AUTODESK INVENTOR PART (.ipt)
format: ipt  version: 2015 (Build 190159000, 159)  size: 452,096 bytes
history: native  units: mm
features: other x24, loft x2, pattern_circular x2, sketch x1
ambient origin geometry x6: Origin, XZ Plane, X Axis, Y Axis, Z Axis, Center Point
bodies: Solid1 (feature_tree)
feature tree (29):
  other  "Top Point"
  other  "Mesh Plane2"
  other  "Teeth Body"
  other  "Start Point"
  other  "Tooth Plane"
  other  "Start Sketch"
  other  "End Point"
  other  "3D Sketch Right"
  other  "End Plane Right"
  loft  "Loft Right"
  pattern_circular  "Circular Pattern Right"  [2 undecoded]
  other  "3D Sketch Left"
  other  "End Plane Left"
  loft  "Loft Left"
  pattern_circular  "Circular Pattern Left"  [2 undecoded]
  other  "Fix Body"
  other  "Mesh Plane"
  other  "Top Plane"
  other  "Teeth Body Sketch"
  other  "End Plane"
  other  "End Sketch"
  other  "Helical Curve Left"
  other  "End Sketch Left"
  other  "Body Sketch"
  sketch  "Sketch6"  dims[d0=16.0mm d1=14.302944mm d2=17.414214mm d3=4.0mm d4=7.292893mm d5=90.0deg d7=4.207475mm d8=4.618655mm d9=9.533471mm d11=4.11mm d12=2.683207mm d15=2.945426mm d16=6.079722mm d17=0.0mm d18=90.0deg d19=0.0mm d20=90.0deg d21=160.0mm d22=360.0deg d26=80.390855mm d27=2.906209mm d28=16.0mm d29=-7.853982mm d30=2.683207mm d31=2.945426mm d32=6.079722mm d35=0.0mm d37=0.0mm d39=0.0mm d40=90.0deg d41=160.0mm d42=360.0deg d46=90.0deg d47=90.0deg d48=0.0mm d49=0.0mm d50=90.0deg d51=1.963495mm d52=0.0mm d53=0.0mm d54=0.0mm d56=3.981101mm d57=12.973708mm d58=9.849708mm d59=8.273644mm d60=6.281394mm d61=8.273644mm d62=6.281394mm d65=80.390855mm d66=31.5mm d67=16.0mm d68=-7.853982mm d69=2.906209mm d70=2.945426mm d71=6.079722mm d72=2.683207mm d73=6.281394mm d74=8.273644mm d75=0.0mm d77=0.0mm d79=0.0mm d80=90.0deg d81=160.0mm d82=360.0deg d84=10.0mm d85=20.0mm d86=20.0mm d87=10.0mm d88=0.0mm d89=0.0mm d90=90.0deg d91=90.0deg d92=90.0deg d93=90.0deg]
  other  "Srf1"
  other  "Helical Curve Right"
  other  "End Sketch Right"
  other  "Pitch Diameter"
note: 4 required parameter values undecoded (feature->parameter linkage not recoverable at this tier; creation-order binding heuristic only, values carry confidence <= 0.55)
